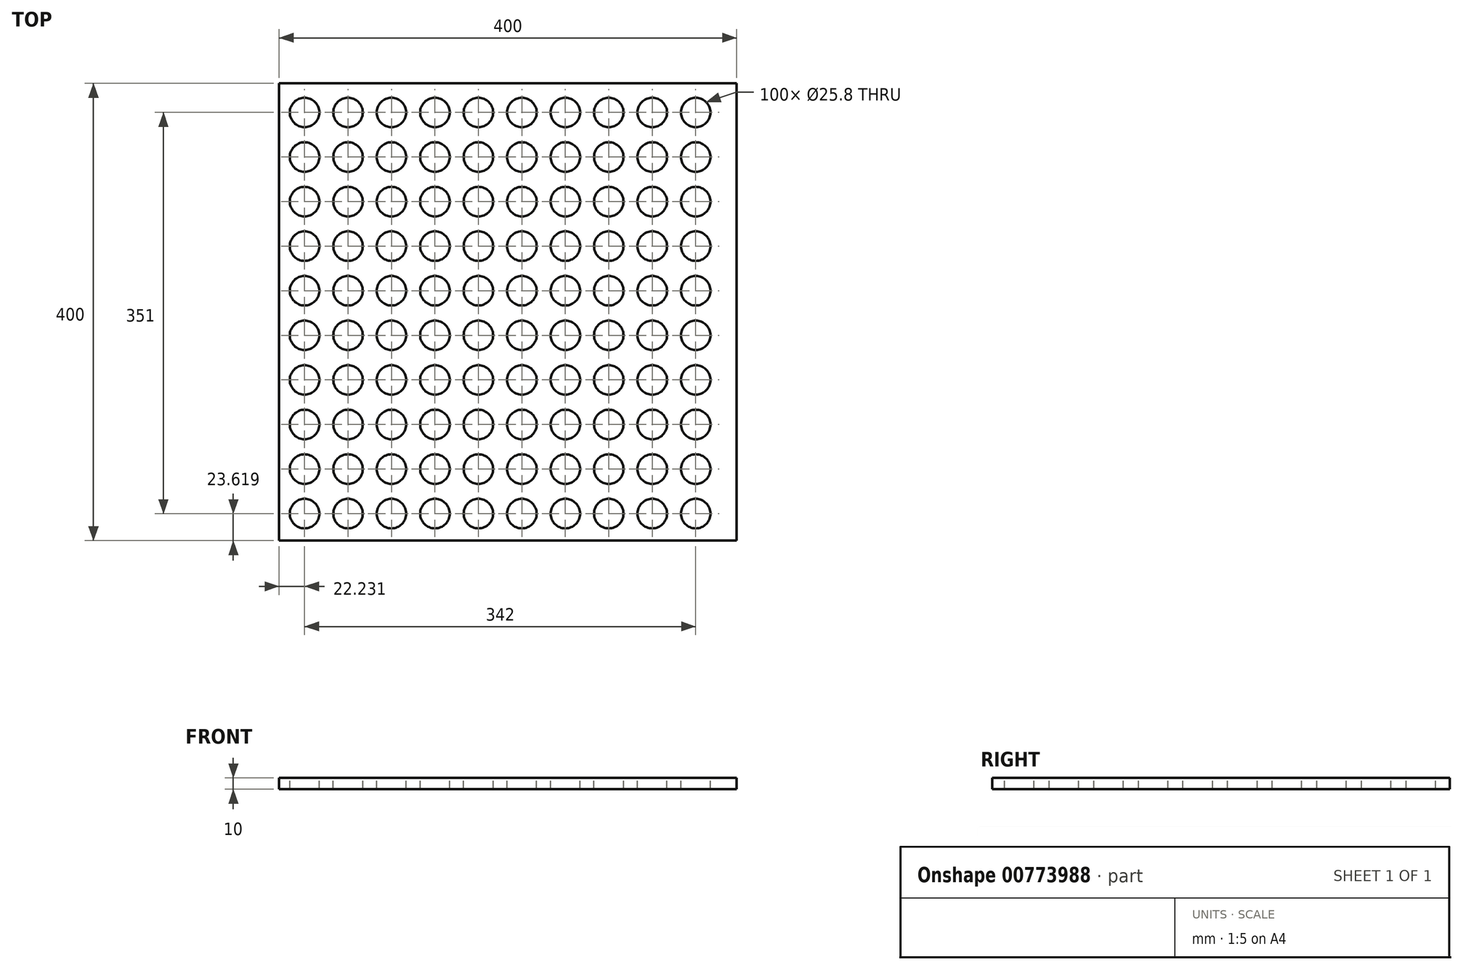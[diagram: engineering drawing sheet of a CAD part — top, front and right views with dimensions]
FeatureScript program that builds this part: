
annotation { "Feature Type Name" : "Feature", "Feature Type Description" : "" }
export const myFeature = defineFeature(function(context is Context, id is Id, definition is map)
    precondition{}
    {
        {
            var Q0;
            Q0=qCreatedBy(makeId("Top.planeOp"),FACE);
            var sketch = newSketch(context, id + "F0", { "sketchPlane" : qUnion([Q0])});
            skLineSegment(sketch, "E0.bottom", {"start": v(-200, 200) * mm, "end": v(200, 200) * mm});
            skLineSegment(sketch, "E0.top", {"start": v(-200, -200) * mm, "end": v(200, -200) * mm});
            skLineSegment(sketch, "E0.left", {"start": v(-200, 200) * mm, "end": v(-200, -200) * mm});
            skLineSegment(sketch, "E0.right", {"start": v(200, 200) * mm, "end": v(200, -200) * mm});
            skPoint(sketch, "E0.middle", {"position": v(0, 0) * mm});
            skSolve(sketch);
        }
        {
            var Q0;
            Q0 = qSketchRegion(id + "F0", true);
            extrude(context, id + "F1", {"entities" : qUnion([Q0]), "depth" : 10 * mm, "offsetDistance" : 25 * mm});
        }
        {
            var Q0;
            Q0=makeQuery(id+"F1.opExtrude","CAP_FACE",FACE,{"disambiguationData":[OSD([sQuery(id+"F0.wireOp",EDGE,"E0.bottom"),sQuery(id+"F0.wireOp",EDGE,"E0.top"),sQuery(id+"F0.wireOp",EDGE,"E0.left"),sQuery(id+"F0.wireOp",EDGE,"E0.right")])],"isStart":false});
            var sketch = newSketch(context, id + "F2", { "sketchPlane" : qUnion([Q0])});
            skCircle(sketch, "E1", {"center": v(164.23, -176.38) * mm, "radius": 12.9 * mm});
            skCircle(sketch, "E2.0.1.0", {"center": v(164.23, -137.38) * mm, "radius": 12.9 * mm});
            skCircle(sketch, "E2.0.2.0", {"center": v(164.23, -98.38) * mm, "radius": 12.9 * mm});
            skCircle(sketch, "E2.0.3.0", {"center": v(164.23, -59.38) * mm, "radius": 12.9 * mm});
            skCircle(sketch, "E2.0.4.0", {"center": v(164.23, -20.38) * mm, "radius": 12.9 * mm});
            skCircle(sketch, "E2.0.5.0", {"center": v(164.23, 18.62) * mm, "radius": 12.9 * mm});
            skCircle(sketch, "E2.0.6.0", {"center": v(164.23, 57.62) * mm, "radius": 12.9 * mm});
            skCircle(sketch, "E2.0.7.0", {"center": v(164.23, 96.62) * mm, "radius": 12.9 * mm});
            skCircle(sketch, "E2.0.8.0", {"center": v(164.23, 135.62) * mm, "radius": 12.9 * mm});
            skCircle(sketch, "E2.0.9.0", {"center": v(164.23, 174.62) * mm, "radius": 12.9 * mm});
            skCircle(sketch, "E2.1.0.0", {"center": v(126.23, -176.38) * mm, "radius": 12.9 * mm});
            skCircle(sketch, "E2.1.1.0", {"center": v(126.23, -137.38) * mm, "radius": 12.9 * mm});
            skCircle(sketch, "E2.1.2.0", {"center": v(126.23, -98.38) * mm, "radius": 12.9 * mm});
            skCircle(sketch, "E2.1.3.0", {"center": v(126.23, -59.38) * mm, "radius": 12.9 * mm});
            skCircle(sketch, "E2.1.4.0", {"center": v(126.23, -20.38) * mm, "radius": 12.9 * mm});
            skCircle(sketch, "E2.1.5.0", {"center": v(126.23, 18.62) * mm, "radius": 12.9 * mm});
            skCircle(sketch, "E2.1.6.0", {"center": v(126.23, 57.62) * mm, "radius": 12.9 * mm});
            skCircle(sketch, "E2.1.7.0", {"center": v(126.23, 96.62) * mm, "radius": 12.9 * mm});
            skCircle(sketch, "E2.1.8.0", {"center": v(126.23, 135.62) * mm, "radius": 12.9 * mm});
            skCircle(sketch, "E2.1.9.0", {"center": v(126.23, 174.62) * mm, "radius": 12.9 * mm});
            skCircle(sketch, "E2.2.0.0", {"center": v(88.23, -176.38) * mm, "radius": 12.9 * mm});
            skCircle(sketch, "E2.2.1.0", {"center": v(88.23, -137.38) * mm, "radius": 12.9 * mm});
            skCircle(sketch, "E2.2.2.0", {"center": v(88.23, -98.38) * mm, "radius": 12.9 * mm});
            skCircle(sketch, "E2.2.3.0", {"center": v(88.23, -59.38) * mm, "radius": 12.9 * mm});
            skCircle(sketch, "E2.2.4.0", {"center": v(88.23, -20.38) * mm, "radius": 12.9 * mm});
            skCircle(sketch, "E2.2.5.0", {"center": v(88.23, 18.62) * mm, "radius": 12.9 * mm});
            skCircle(sketch, "E2.2.6.0", {"center": v(88.23, 57.62) * mm, "radius": 12.9 * mm});
            skCircle(sketch, "E2.2.7.0", {"center": v(88.23, 96.62) * mm, "radius": 12.9 * mm});
            skCircle(sketch, "E2.2.8.0", {"center": v(88.23, 135.62) * mm, "radius": 12.9 * mm});
            skCircle(sketch, "E2.2.9.0", {"center": v(88.23, 174.62) * mm, "radius": 12.9 * mm});
            skCircle(sketch, "E2.3.0.0", {"center": v(50.23, -176.38) * mm, "radius": 12.9 * mm});
            skCircle(sketch, "E2.3.1.0", {"center": v(50.23, -137.38) * mm, "radius": 12.9 * mm});
            skCircle(sketch, "E2.3.2.0", {"center": v(50.23, -98.38) * mm, "radius": 12.9 * mm});
            skCircle(sketch, "E2.3.3.0", {"center": v(50.23, -59.38) * mm, "radius": 12.9 * mm});
            skCircle(sketch, "E2.3.4.0", {"center": v(50.23, -20.38) * mm, "radius": 12.9 * mm});
            skCircle(sketch, "E2.3.5.0", {"center": v(50.23, 18.62) * mm, "radius": 12.9 * mm});
            skCircle(sketch, "E2.3.6.0", {"center": v(50.23, 57.62) * mm, "radius": 12.9 * mm});
            skCircle(sketch, "E2.3.7.0", {"center": v(50.23, 96.62) * mm, "radius": 12.9 * mm});
            skCircle(sketch, "E2.3.8.0", {"center": v(50.23, 135.62) * mm, "radius": 12.9 * mm});
            skCircle(sketch, "E2.3.9.0", {"center": v(50.23, 174.62) * mm, "radius": 12.9 * mm});
            skCircle(sketch, "E2.4.0.0", {"center": v(12.23, -176.38) * mm, "radius": 12.9 * mm});
            skCircle(sketch, "E2.4.1.0", {"center": v(12.23, -137.38) * mm, "radius": 12.9 * mm});
            skCircle(sketch, "E2.4.2.0", {"center": v(12.23, -98.38) * mm, "radius": 12.9 * mm});
            skCircle(sketch, "E2.4.3.0", {"center": v(12.23, -59.38) * mm, "radius": 12.9 * mm});
            skCircle(sketch, "E2.4.4.0", {"center": v(12.23, -20.38) * mm, "radius": 12.9 * mm});
            skCircle(sketch, "E2.4.5.0", {"center": v(12.23, 18.62) * mm, "radius": 12.9 * mm});
            skCircle(sketch, "E2.4.6.0", {"center": v(12.23, 57.62) * mm, "radius": 12.9 * mm});
            skCircle(sketch, "E2.4.7.0", {"center": v(12.23, 96.62) * mm, "radius": 12.9 * mm});
            skCircle(sketch, "E2.4.8.0", {"center": v(12.23, 135.62) * mm, "radius": 12.9 * mm});
            skCircle(sketch, "E2.4.9.0", {"center": v(12.23, 174.62) * mm, "radius": 12.9 * mm});
            skCircle(sketch, "E2.5.0.0", {"center": v(-25.77, -176.38) * mm, "radius": 12.9 * mm});
            skCircle(sketch, "E2.5.1.0", {"center": v(-25.77, -137.38) * mm, "radius": 12.9 * mm});
            skCircle(sketch, "E2.5.2.0", {"center": v(-25.77, -98.38) * mm, "radius": 12.9 * mm});
            skCircle(sketch, "E2.5.3.0", {"center": v(-25.77, -59.38) * mm, "radius": 12.9 * mm});
            skCircle(sketch, "E2.5.4.0", {"center": v(-25.77, -20.38) * mm, "radius": 12.9 * mm});
            skCircle(sketch, "E2.5.5.0", {"center": v(-25.77, 18.62) * mm, "radius": 12.9 * mm});
            skCircle(sketch, "E2.5.6.0", {"center": v(-25.77, 57.62) * mm, "radius": 12.9 * mm});
            skCircle(sketch, "E2.5.7.0", {"center": v(-25.77, 96.62) * mm, "radius": 12.9 * mm});
            skCircle(sketch, "E2.5.8.0", {"center": v(-25.77, 135.62) * mm, "radius": 12.9 * mm});
            skCircle(sketch, "E2.5.9.0", {"center": v(-25.77, 174.62) * mm, "radius": 12.9 * mm});
            skCircle(sketch, "E2.6.0.0", {"center": v(-63.77, -176.38) * mm, "radius": 12.9 * mm});
            skCircle(sketch, "E2.6.1.0", {"center": v(-63.77, -137.38) * mm, "radius": 12.9 * mm});
            skCircle(sketch, "E2.6.2.0", {"center": v(-63.77, -98.38) * mm, "radius": 12.9 * mm});
            skCircle(sketch, "E2.6.3.0", {"center": v(-63.77, -59.38) * mm, "radius": 12.9 * mm});
            skCircle(sketch, "E2.6.4.0", {"center": v(-63.77, -20.38) * mm, "radius": 12.9 * mm});
            skCircle(sketch, "E2.6.5.0", {"center": v(-63.77, 18.62) * mm, "radius": 12.9 * mm});
            skCircle(sketch, "E2.6.6.0", {"center": v(-63.77, 57.62) * mm, "radius": 12.9 * mm});
            skCircle(sketch, "E2.6.7.0", {"center": v(-63.77, 96.62) * mm, "radius": 12.9 * mm});
            skCircle(sketch, "E2.6.8.0", {"center": v(-63.77, 135.62) * mm, "radius": 12.9 * mm});
            skCircle(sketch, "E2.6.9.0", {"center": v(-63.77, 174.62) * mm, "radius": 12.9 * mm});
            skCircle(sketch, "E2.7.0.0", {"center": v(-101.77, -176.38) * mm, "radius": 12.9 * mm});
            skCircle(sketch, "E2.7.1.0", {"center": v(-101.77, -137.38) * mm, "radius": 12.9 * mm});
            skCircle(sketch, "E2.7.2.0", {"center": v(-101.77, -98.38) * mm, "radius": 12.9 * mm});
            skCircle(sketch, "E2.7.3.0", {"center": v(-101.77, -59.38) * mm, "radius": 12.9 * mm});
            skCircle(sketch, "E2.7.4.0", {"center": v(-101.77, -20.38) * mm, "radius": 12.9 * mm});
            skCircle(sketch, "E2.7.5.0", {"center": v(-101.77, 18.62) * mm, "radius": 12.9 * mm});
            skCircle(sketch, "E2.7.6.0", {"center": v(-101.77, 57.62) * mm, "radius": 12.9 * mm});
            skCircle(sketch, "E2.7.7.0", {"center": v(-101.77, 96.62) * mm, "radius": 12.9 * mm});
            skCircle(sketch, "E2.7.8.0", {"center": v(-101.77, 135.62) * mm, "radius": 12.9 * mm});
            skCircle(sketch, "E2.7.9.0", {"center": v(-101.77, 174.62) * mm, "radius": 12.9 * mm});
            skCircle(sketch, "E2.8.0.0", {"center": v(-139.77, -176.38) * mm, "radius": 12.9 * mm});
            skCircle(sketch, "E2.8.1.0", {"center": v(-139.77, -137.38) * mm, "radius": 12.9 * mm});
            skCircle(sketch, "E2.8.2.0", {"center": v(-139.77, -98.38) * mm, "radius": 12.9 * mm});
            skCircle(sketch, "E2.8.3.0", {"center": v(-139.77, -59.38) * mm, "radius": 12.9 * mm});
            skCircle(sketch, "E2.8.4.0", {"center": v(-139.77, -20.38) * mm, "radius": 12.9 * mm});
            skCircle(sketch, "E2.8.5.0", {"center": v(-139.77, 18.62) * mm, "radius": 12.9 * mm});
            skCircle(sketch, "E2.8.6.0", {"center": v(-139.77, 57.62) * mm, "radius": 12.9 * mm});
            skCircle(sketch, "E2.8.7.0", {"center": v(-139.77, 96.62) * mm, "radius": 12.9 * mm});
            skCircle(sketch, "E2.8.8.0", {"center": v(-139.77, 135.62) * mm, "radius": 12.9 * mm});
            skCircle(sketch, "E2.8.9.0", {"center": v(-139.77, 174.62) * mm, "radius": 12.9 * mm});
            skCircle(sketch, "E2.9.0.0", {"center": v(-177.77, -176.38) * mm, "radius": 12.9 * mm});
            skCircle(sketch, "E2.9.1.0", {"center": v(-177.77, -137.38) * mm, "radius": 12.9 * mm});
            skCircle(sketch, "E2.9.2.0", {"center": v(-177.77, -98.38) * mm, "radius": 12.9 * mm});
            skCircle(sketch, "E2.9.3.0", {"center": v(-177.77, -59.38) * mm, "radius": 12.9 * mm});
            skCircle(sketch, "E2.9.4.0", {"center": v(-177.77, -20.38) * mm, "radius": 12.9 * mm});
            skCircle(sketch, "E2.9.5.0", {"center": v(-177.77, 18.62) * mm, "radius": 12.9 * mm});
            skCircle(sketch, "E2.9.6.0", {"center": v(-177.77, 57.62) * mm, "radius": 12.9 * mm});
            skCircle(sketch, "E2.9.7.0", {"center": v(-177.77, 96.62) * mm, "radius": 12.9 * mm});
            skCircle(sketch, "E2.9.8.0", {"center": v(-177.77, 135.62) * mm, "radius": 12.9 * mm});
            skCircle(sketch, "E2.9.9.0", {"center": v(-177.77, 174.62) * mm, "radius": 12.9 * mm});
            skLineSegment(sketch, "E2.direction1", {"start": v(164.23, -176.38) * mm, "end": v(126.23, -176.38) * mm, "construction": true});
            skLineSegment(sketch, "E2.direction2", {"start": v(164.23, -176.38) * mm, "end": v(164.23, -137.38) * mm, "construction": true});
            skSolve(sketch);
        }
        {
            var Q0;
            Q0 = qSketchRegion(id + "F2", true);
            extrude(context, id + "F3", {"entities" : qUnion([Q0]), "operationType" : NewBodyOperationType.REMOVE, "oppositeDirection" : true, "depth" : 13 * mm, "offsetDistance" : 25 * mm});
        }
    });
